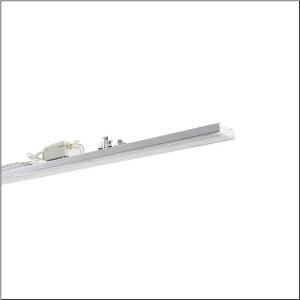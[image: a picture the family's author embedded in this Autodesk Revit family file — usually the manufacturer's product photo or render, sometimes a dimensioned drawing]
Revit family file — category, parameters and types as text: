
# Revit family: licross_r__11_recessed_ho_51tl12cn46xm_c9e3
name_source: partatom
category: Lighting Fixtures
units: mm (PartAtom-declared; Revit-internal decimal feet)

## family parameters
Cut with Voids When Loaded = No
Host = Face
Light Source = No
Part Type = Normal
Room Calculation Point = No
Round Connector Dimension = Use Diameter
Shared = No

## types (1)
- --- (1 x LED, 6020 lm, 30.1 W, 4000K)
    Apparent Load = 30 VA
    CIE Flux Codes = 66 91 98 100 100
    Color Rendering = 80
    Color Temperature = 4000K
    Default Elevation = 1800 mm
    Description = Licross® 11 Recessed HO, luminaire insert, of sheet steel, coil coated, white, length: 1.500mm, width: 66mm, height: 67mm, LED rated luminous flux: 6.020lm, light colour: 840, SDCM (Standard Deviation of Colour Matching)MacAdam ≤ 2 SDCM (initial), control gear: ON/OFF Multilumen, CLOi, with plug, 3-pole, with phase selection, mains connection: 220..240V, AC, 50/60Hz, start of lifetime: 30W, end of service life: 33W, internal wiring halogen-free, primary optical cover: cover, of PMMA, light emission: direct distribution, primary light characteristic: symmetric, protection rating (complete): IP40, insulation class (complete): insulation class I (protective earthing), certification: CE, ENEC, VDE, UKCA, protection symbol: D if used in an environment without relevant dust loads with corresponding accessories, impact resistance: IK06, permissible ambient temperature for indoor applications: -35..+50°C, corresponds to IFS (International Featured Standards) requirements for safety and quality in the food industry, reducing of maximum allowable ambient temperature of 5°C with ceiling mounting, LABS conformity tested according to VDMA 24364:2018-05, packaging unit: 1 piece
    Height = 58 mm
    Lamp = 1 x LED
    Lamp Light Flux = 6020 lm
    Lamp Power = 30.1 W
    Lamp count = 1
    Length = 1500 mm
    Luminous efficacy = 200 lm/W
    Manufacturer = Siteco
    ModVariant = No
    Model = 51TL12CN46XM
    Mounting Place = Ceiling
    Mounting Type = Pendant
    Number of Poles = 1
    OnlyDefault = Yes
    Power Factor = 1
    Product Name = Licross® 11 Recessed HO
    Product group = luminaire insert | ceiling pendant
    ProductGroupID = 901
    Protection Class = Protection class I
    Protection Degree = IP 40
    RLX_Detail_Level = 1
    RLX_Emergency_Light_Flux = 0 lm
    RLX_Emergency_Type = 0
    RLX_Emergency_Type_DB = No
    RlxData = <blob elided: 22241 chars, md5=e88d7efa>
    Socket = socket
    Standby Power = 0 W
    System Light Flux = 6020 lm
    System Power = 30 W
    Type Comments = factory setting: luminous flux: 100 % | (A | C | E) | 71 mA
    Type Image = l_1296930.jpg
    URL = http://relux.com
    VarID = @adj_092765
    Voltage = 0 V
    Weight = 0.00 kg
    Width = 66 mm

## geometry (parser evidence)
native form markers: Blend x4, Sweep x12
no freeform markers — native parametric forms only
